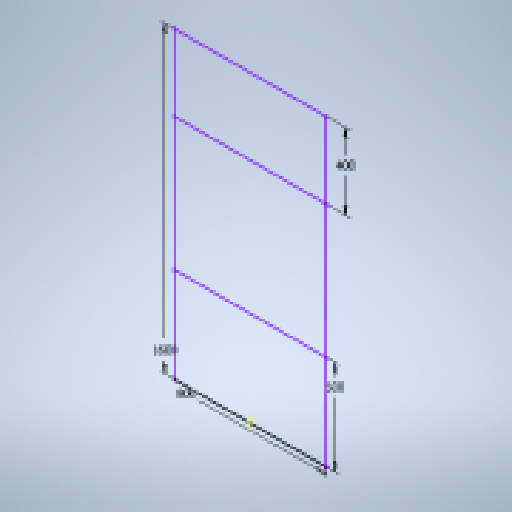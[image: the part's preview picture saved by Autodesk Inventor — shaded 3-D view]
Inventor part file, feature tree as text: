
AUTODESK INVENTOR PART (.ipt)
format: ipt  version: 2025 (Build 290162010, 162A)  size: 133,632 bytes
history: native  units: in
note: dims shown in document units (in); Inventor stores cm internally (conversion verified against a paired STEP export)
features: sketch x2
ambient origin geometry x8: Origin, YZ Plane, XZ Plane, XY Plane, X Axis, Y Axis, Z Axis, Center Point
feature tree (2):
  sketch  "Sketch3"  dims[d5=7.874in d6=59.0551in d7=19.685in d10=19.685in]
  sketch  "3D Sketch3"
